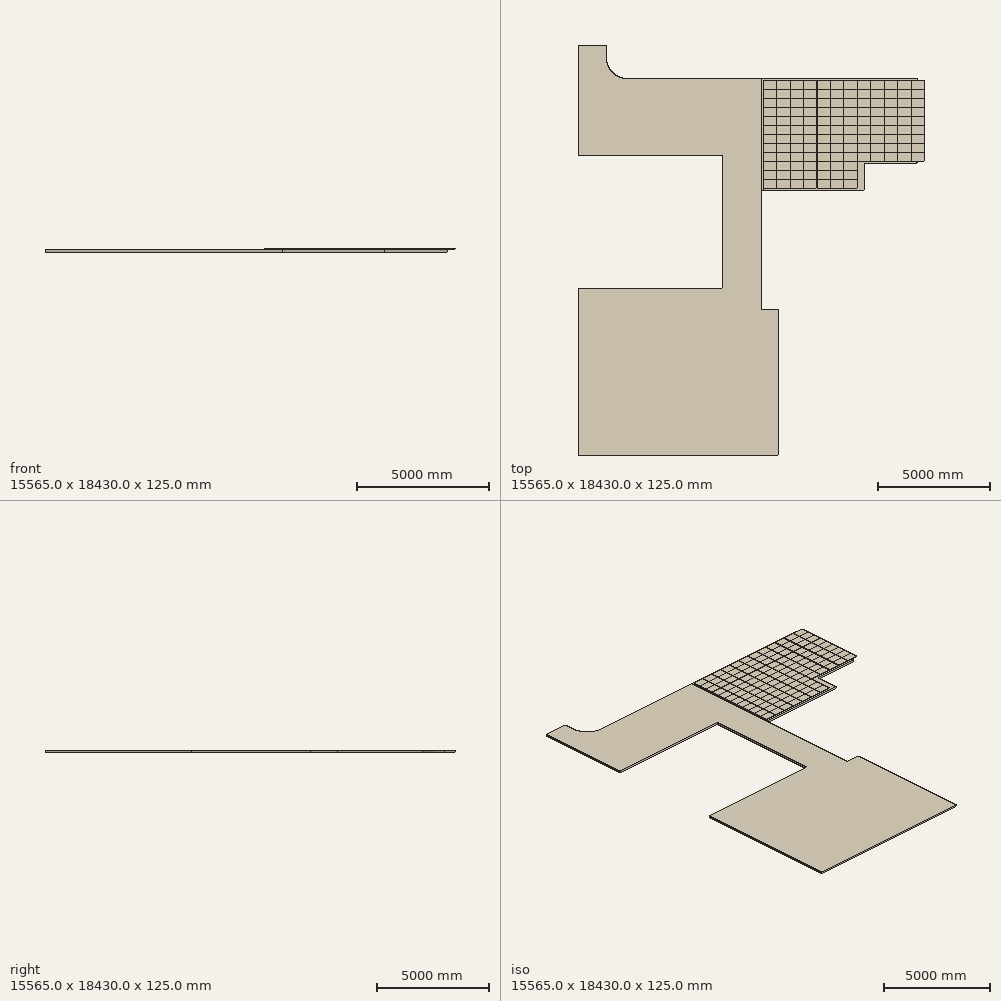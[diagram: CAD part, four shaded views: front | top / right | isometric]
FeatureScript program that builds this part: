
annotation { "Feature Type Name" : "Feature", "Feature Type Description" : "" }
export const myFeature = defineFeature(function(context is Context, id is Id, definition is map)
    precondition{}
    {
        {
            var Q0;
            Q0=qCreatedBy(makeId("Top.planeOp"),FACE);
            var sketch = newSketch(context, id + "F0", { "sketchPlane" : qUnion([Q0])});
            skLineSegment(sketch, "E0.bottom", {"start": v(1925, 8965) * mm, "end": v(-11075, 8965) * mm});
            skLineSegment(sketch, "E0.top", {"start": v(1925, 3965) * mm, "end": v(-5075, 3965) * mm});
            skLineSegment(sketch, "E0.left", {"start": v(1925, 8965) * mm, "end": v(1925, 3965) * mm});
            skLineSegment(sketch, "E0.right", {"start": v(-5075, 3965) * mm, "end": v(-5075, -1415) * mm});
            skLineSegment(sketch, "E1", {"start": v(-6825, 5535) * mm, "end": v(-6825, -465) * mm});
            skLineSegment(sketch, "E2", {"start": v(-4325, -1415) * mm, "end": v(-4325, -7965) * mm});
            skLineSegment(sketch, "E3", {"start": v(-4325, -7965) * mm, "end": v(-13325, -7965) * mm});
            skLineSegment(sketch, "E4", {"start": v(-13325, -7965) * mm, "end": v(-13325, -465) * mm});
            skLineSegment(sketch, "E5", {"start": v(-13325, -465) * mm, "end": v(-6825, -465) * mm});
            skLineSegment(sketch, "E6", {"start": v(-4325, -1415) * mm, "end": v(-5075, -1415) * mm});
            skLineSegment(sketch, "E7.top", {"start": v(-6825, 5535) * mm, "end": v(-13325, 5535) * mm});
            skLineSegment(sketch, "E8", {"start": v(-13325, 5535) * mm, "end": v(-13325, 10465) * mm});
            skLineSegment(sketch, "E9", {"start": v(-12075, 9965) * mm, "end": v(-12075, 10465) * mm});
            skLineSegment(sketch, "E10", {"start": v(-12075, 10465) * mm, "end": v(-13325, 10465) * mm});
            skPoint(sketch, "E11.0.visualSharp", {"position": v(-12075, 8965) * mm});
            skArc(sketch, "E11.0.filletArc", {"start": v(-12075, 9965) * mm, "mid": v(-11782.1, 9257.9) * mm, "end": v(-11075, 8965) * mm});
            skSolve(sketch);
        }
        {
            var Q0;
            Q0=makeQuery(id+"F0.imprint","IMPRINT",FACE,{"disambiguationData":[TD([[makeQuery(id+"F0.imprint","IMPRINT",EDGE,{"derivedFrom":sQuery(id+"F0.wireOp",EDGE,"E0.bottom")}),1.0]])]});
            extrude(context, id + "F1", {"entities" : qUnion([Q0]), "oppositeDirection" : true, "depth" : 100 * mm});
        }
        {
            var Q0;
            Q0=makeQuery(id+"F1.opExtrude","CAP_FACE",FACE,{"disambiguationData":[OSD([sQuery(id+"F0.wireOp",EDGE,"E0.bottom"),sQuery(id+"F0.wireOp",EDGE,"E0.top"),sQuery(id+"F0.wireOp",EDGE,"E0.left"),sQuery(id+"F0.wireOp",EDGE,"E0.right"),sQuery(id+"F0.wireOp",EDGE,"uScAsCd1-O7hj-DaH3-3mnT-VNKRzyi0iVPP"),sQuery(id+"F0.wireOp",EDGE,"ugRH4nXX-NC2v-Y8Qp-Eb5w-qthfwM3VaUrv"),sQuery(id+"F0.wireOp",EDGE,"aPtSS9E7-FlIR-lzfM-v5Z0-DnZjgckhtP2z")])],"isStart":true});
            var sketch = newSketch(context, id + "F2", { "sketchPlane" : qUnion([Q0])});
            skLineSegment(sketch, "E12.bottom", {"start": v(1925, 3965) * mm, "end": v(-450, 3965) * mm});
            skLineSegment(sketch, "E12.top", {"start": v(1925, 5165) * mm, "end": v(-450, 5165) * mm});
            skLineSegment(sketch, "E12.left", {"start": v(1925, 3965) * mm, "end": v(1925, 5165) * mm});
            skLineSegment(sketch, "E12.right", {"start": v(-450, 3965) * mm, "end": v(-450, 5165) * mm});
            skSolve(sketch);
        }
        {
            var Q0;
            Q0=makeQuery(id+"F2.imprint","IMPRINT",FACE,{"disambiguationData":[TD([[makeQuery(id+"F2.imprint","IMPRINT",EDGE,{"derivedFrom":sQuery(id+"F2.wireOp",EDGE,"E12.bottom")}),-1.0]])]});
            extrude(context, id + "F3", {"entities" : qUnion([Q0]), "operationType" : NewBodyOperationType.REMOVE, "endBound" : BoundingType.UP_TO_NEXT, "oppositeDirection" : true, "depth" : 25 * mm});
        }
        {
            var Q0;
            Q0=makeQuery(id+"F1.opExtrude","CAP_FACE",FACE,{"disambiguationData":[OSD([sQuery(id+"F0.wireOp",EDGE,"E0.bottom"),sQuery(id+"F0.wireOp",EDGE,"E0.top"),sQuery(id+"F0.wireOp",EDGE,"E0.left"),sQuery(id+"F0.wireOp",EDGE,"E0.right"),sQuery(id+"F0.wireOp",EDGE,"E1"),sQuery(id+"F0.wireOp",EDGE,"E2"),sQuery(id+"F0.wireOp",EDGE,"E3"),sQuery(id+"F0.wireOp",EDGE,"E4"),sQuery(id+"F0.wireOp",EDGE,"E5"),sQuery(id+"F0.wireOp",EDGE,"E6"),sQuery(id+"F0.wireOp",EDGE,"IaO83Gh2-lnCz-rkBB-go4h-1UUhoPdXk0SL"),sQuery(id+"F0.wireOp",EDGE,"E7.bottom"),sQuery(id+"F0.wireOp",EDGE,"E7.top"),sQuery(id+"F0.wireOp",EDGE,"E7.right")])],"isStart":true});
            var sketch = newSketch(context, id + "F4", { "sketchPlane" : qUnion([Q0])});
            skLineSegment(sketch, "E13.bottom", {"start": v(-5075, 8965) * mm, "end": v(1925, 8965) * mm});
            skLineSegment(sketch, "E14.bottom", {"start": v(1925, 5165) * mm, "end": v(1865, 5165) * mm});
            skLineSegment(sketch, "E14.left", {"start": v(1925, 5165) * mm, "end": v(1925, 8965) * mm});
            skLineSegment(sketch, "E14.right", {"start": v(1865, 5165) * mm, "end": v(1865, 8905) * mm});
            skLineSegment(sketch, "E15.bottom", {"start": v(-5075, 3965) * mm, "end": v(-5015, 3965) * mm});
            skLineSegment(sketch, "E15.left", {"start": v(-5075, 3965) * mm, "end": v(-5075, 8965) * mm});
            skLineSegment(sketch, "E15.right", {"start": v(-5015, 3965) * mm, "end": v(-5015, 8905) * mm});
            skLineSegment(sketch, "E16.trimOffspring", {"start": v(-5015, 8905) * mm, "end": v(1865, 8905) * mm});
            skSolve(sketch);
        }
        {
            var Q0;
            Q0 = qSketchRegion(id + "F4", true);
            extrude(context, id + "F5", {"entities" : qUnion([Q0]), "operationType" : NewBodyOperationType.ADD, "depth" : 5 * mm});
        }
        {
            var Q0;
            {var subQ0=sQuery(id+"F0.wireOp",EDGE,"E0.top");Q0=makeQuery(id+"F5.boolean.opBoolean","SPLIT",FACE,{"disambiguationData":[TD([makeQuery(id+"F3.boolean.opBoolean","COPY",FACE,{"derivedFrom":makeQuery(id+"F3.opExtrude","SWEPT_FACE",FACE,{"disambiguationData":[OSD([sQuery(id+"F2.wireOp",EDGE,"E12.top")])]})})])],"derivedFrom":makeQuery(id+"F1.opExtrude","CAP_FACE",FACE,{"disambiguationData":[OSD([sQuery(id+"F0.wireOp",EDGE,"E0.bottom"),subQ0,sQuery(id+"F0.wireOp",EDGE,"E0.left"),sQuery(id+"F0.wireOp",EDGE,"E0.right"),sQuery(id+"F0.wireOp",EDGE,"E1"),sQuery(id+"F0.wireOp",EDGE,"E2"),sQuery(id+"F0.wireOp",EDGE,"E3"),sQuery(id+"F0.wireOp",EDGE,"E4"),sQuery(id+"F0.wireOp",EDGE,"E5"),sQuery(id+"F0.wireOp",EDGE,"E6"),sQuery(id+"F0.wireOp",EDGE,"E7.top"),sQuery(id+"F0.wireOp",EDGE,"AURVtqG8-NIB2-Ryh4-XiBF-dMKONcv7BB0R"),sQuery(id+"F0.wireOp",EDGE,"Tb1P3ruf-0xxy-VXF0-uDJz-wuIkWxFJXR6I"),sQuery(id+"F0.wireOp",EDGE,"E8")])],"isStart":true})});}
            var sketch = newSketch(context, id + "F6", { "sketchPlane" : qUnion([Q0])});
            skLineSegment(sketch, "E17.bottom", {"start": v(-5015, 8905) * mm, "end": v(-4415, 8905) * mm});
            skLineSegment(sketch, "E17.top", {"start": v(-5015, 8505) * mm, "end": v(-4415, 8505) * mm});
            skLineSegment(sketch, "E17.left", {"start": v(-5015, 8905) * mm, "end": v(-5015, 8505) * mm});
            skLineSegment(sketch, "E17.right", {"start": v(-4415, 8905) * mm, "end": v(-4415, 8505) * mm});
            skLineSegment(sketch, "E18.0.1.0", {"start": v(-5015, 8500) * mm, "end": v(-4415, 8500) * mm});
            skLineSegment(sketch, "E18.0.1.1", {"start": v(-5015, 8100) * mm, "end": v(-4415, 8100) * mm});
            skLineSegment(sketch, "E18.0.1.2", {"start": v(-5015, 8500) * mm, "end": v(-5015, 8100) * mm});
            skLineSegment(sketch, "E18.0.1.3", {"start": v(-4415, 8500) * mm, "end": v(-4415, 8100) * mm});
            skLineSegment(sketch, "E18.0.2.0", {"start": v(-5015, 8095) * mm, "end": v(-4415, 8095) * mm});
            skLineSegment(sketch, "E18.0.2.1", {"start": v(-5015, 7695) * mm, "end": v(-4415, 7695) * mm});
            skLineSegment(sketch, "E18.0.2.2", {"start": v(-5015, 8095) * mm, "end": v(-5015, 7695) * mm});
            skLineSegment(sketch, "E18.0.2.3", {"start": v(-4415, 8095) * mm, "end": v(-4415, 7695) * mm});
            skLineSegment(sketch, "E18.0.3.0", {"start": v(-5015, 7690) * mm, "end": v(-4415, 7690) * mm});
            skLineSegment(sketch, "E18.0.3.1", {"start": v(-5015, 7290) * mm, "end": v(-4415, 7290) * mm});
            skLineSegment(sketch, "E18.0.3.2", {"start": v(-5015, 7690) * mm, "end": v(-5015, 7290) * mm});
            skLineSegment(sketch, "E18.0.3.3", {"start": v(-4415, 7690) * mm, "end": v(-4415, 7290) * mm});
            skLineSegment(sketch, "E18.0.4.0", {"start": v(-5015, 7285) * mm, "end": v(-4415, 7285) * mm});
            skLineSegment(sketch, "E18.0.4.1", {"start": v(-5015, 6885) * mm, "end": v(-4415, 6885) * mm});
            skLineSegment(sketch, "E18.0.4.2", {"start": v(-5015, 7285) * mm, "end": v(-5015, 6885) * mm});
            skLineSegment(sketch, "E18.0.4.3", {"start": v(-4415, 7285) * mm, "end": v(-4415, 6885) * mm});
            skLineSegment(sketch, "E18.0.5.0", {"start": v(-5015, 6880) * mm, "end": v(-4415, 6880) * mm});
            skLineSegment(sketch, "E18.0.5.1", {"start": v(-5015, 6480) * mm, "end": v(-4415, 6480) * mm});
            skLineSegment(sketch, "E18.0.5.2", {"start": v(-5015, 6880) * mm, "end": v(-5015, 6480) * mm});
            skLineSegment(sketch, "E18.0.5.3", {"start": v(-4415, 6880) * mm, "end": v(-4415, 6480) * mm});
            skLineSegment(sketch, "E18.0.6.0", {"start": v(-5015, 6475) * mm, "end": v(-4415, 6475) * mm});
            skLineSegment(sketch, "E18.0.6.1", {"start": v(-5015, 6075) * mm, "end": v(-4415, 6075) * mm});
            skLineSegment(sketch, "E18.0.6.2", {"start": v(-5015, 6475) * mm, "end": v(-5015, 6075) * mm});
            skLineSegment(sketch, "E18.0.6.3", {"start": v(-4415, 6475) * mm, "end": v(-4415, 6075) * mm});
            skLineSegment(sketch, "E18.0.7.0", {"start": v(-5015, 6070) * mm, "end": v(-4415, 6070) * mm});
            skLineSegment(sketch, "E18.0.7.1", {"start": v(-5015, 5670) * mm, "end": v(-4415, 5670) * mm});
            skLineSegment(sketch, "E18.0.7.2", {"start": v(-5015, 6070) * mm, "end": v(-5015, 5670) * mm});
            skLineSegment(sketch, "E18.0.7.3", {"start": v(-4415, 6070) * mm, "end": v(-4415, 5670) * mm});
            skLineSegment(sketch, "E18.0.8.0", {"start": v(-5015, 5665) * mm, "end": v(-4415, 5665) * mm});
            skLineSegment(sketch, "E18.0.8.1", {"start": v(-5015, 5265) * mm, "end": v(-4415, 5265) * mm});
            skLineSegment(sketch, "E18.0.8.2", {"start": v(-5015, 5665) * mm, "end": v(-5015, 5265) * mm});
            skLineSegment(sketch, "E18.0.8.3", {"start": v(-4415, 5665) * mm, "end": v(-4415, 5265) * mm});
            skLineSegment(sketch, "E18.0.9.0", {"start": v(-5015, 5260) * mm, "end": v(-4415, 5260) * mm});
            skLineSegment(sketch, "E18.0.9.1", {"start": v(-5015, 4860) * mm, "end": v(-4415, 4860) * mm});
            skLineSegment(sketch, "E18.0.9.2", {"start": v(-5015, 5260) * mm, "end": v(-5015, 4860) * mm});
            skLineSegment(sketch, "E18.0.9.3", {"start": v(-4415, 5260) * mm, "end": v(-4415, 4860) * mm});
            skLineSegment(sketch, "E18.0.10.0", {"start": v(-5015, 4855) * mm, "end": v(-4415, 4855) * mm});
            skLineSegment(sketch, "E18.0.10.1", {"start": v(-5015, 4455) * mm, "end": v(-4415, 4455) * mm});
            skLineSegment(sketch, "E18.0.10.2", {"start": v(-5015, 4855) * mm, "end": v(-5015, 4455) * mm});
            skLineSegment(sketch, "E18.0.10.3", {"start": v(-4415, 4855) * mm, "end": v(-4415, 4455) * mm});
            skLineSegment(sketch, "E18.0.11.0", {"start": v(-5015, 4450) * mm, "end": v(-4415, 4450) * mm});
            skLineSegment(sketch, "E18.0.11.1", {"start": v(-5015, 4050) * mm, "end": v(-4415, 4050) * mm});
            skLineSegment(sketch, "E18.0.11.2", {"start": v(-5015, 4450) * mm, "end": v(-5015, 4050) * mm});
            skLineSegment(sketch, "E18.0.11.3", {"start": v(-4415, 4450) * mm, "end": v(-4415, 4050) * mm});
            skLineSegment(sketch, "E18.1.0.0", {"start": v(-4410, 8905) * mm, "end": v(-3810, 8905) * mm});
            skLineSegment(sketch, "E18.1.0.1", {"start": v(-4410, 8505) * mm, "end": v(-3810, 8505) * mm});
            skLineSegment(sketch, "E18.1.0.2", {"start": v(-4410, 8905) * mm, "end": v(-4410, 8505) * mm});
            skLineSegment(sketch, "E18.1.0.3", {"start": v(-3810, 8905) * mm, "end": v(-3810, 8505) * mm});
            skLineSegment(sketch, "E18.1.1.0", {"start": v(-4410, 8500) * mm, "end": v(-3810, 8500) * mm});
            skLineSegment(sketch, "E18.1.1.1", {"start": v(-4410, 8100) * mm, "end": v(-3810, 8100) * mm});
            skLineSegment(sketch, "E18.1.1.2", {"start": v(-4410, 8500) * mm, "end": v(-4410, 8100) * mm});
            skLineSegment(sketch, "E18.1.1.3", {"start": v(-3810, 8500) * mm, "end": v(-3810, 8100) * mm});
            skLineSegment(sketch, "E18.1.2.0", {"start": v(-4410, 8095) * mm, "end": v(-3810, 8095) * mm});
            skLineSegment(sketch, "E18.1.2.1", {"start": v(-4410, 7695) * mm, "end": v(-3810, 7695) * mm});
            skLineSegment(sketch, "E18.1.2.2", {"start": v(-4410, 8095) * mm, "end": v(-4410, 7695) * mm});
            skLineSegment(sketch, "E18.1.2.3", {"start": v(-3810, 8095) * mm, "end": v(-3810, 7695) * mm});
            skLineSegment(sketch, "E18.1.3.0", {"start": v(-4410, 7690) * mm, "end": v(-3810, 7690) * mm});
            skLineSegment(sketch, "E18.1.3.1", {"start": v(-4410, 7290) * mm, "end": v(-3810, 7290) * mm});
            skLineSegment(sketch, "E18.1.3.2", {"start": v(-4410, 7690) * mm, "end": v(-4410, 7290) * mm});
            skLineSegment(sketch, "E18.1.3.3", {"start": v(-3810, 7690) * mm, "end": v(-3810, 7290) * mm});
            skLineSegment(sketch, "E18.1.4.0", {"start": v(-4410, 7285) * mm, "end": v(-3810, 7285) * mm});
            skLineSegment(sketch, "E18.1.4.1", {"start": v(-4410, 6885) * mm, "end": v(-3810, 6885) * mm});
            skLineSegment(sketch, "E18.1.4.2", {"start": v(-4410, 7285) * mm, "end": v(-4410, 6885) * mm});
            skLineSegment(sketch, "E18.1.4.3", {"start": v(-3810, 7285) * mm, "end": v(-3810, 6885) * mm});
            skLineSegment(sketch, "E18.1.5.0", {"start": v(-4410, 6880) * mm, "end": v(-3810, 6880) * mm});
            skLineSegment(sketch, "E18.1.5.1", {"start": v(-4410, 6480) * mm, "end": v(-3810, 6480) * mm});
            skLineSegment(sketch, "E18.1.5.2", {"start": v(-4410, 6880) * mm, "end": v(-4410, 6480) * mm});
            skLineSegment(sketch, "E18.1.5.3", {"start": v(-3810, 6880) * mm, "end": v(-3810, 6480) * mm});
            skLineSegment(sketch, "E18.1.6.0", {"start": v(-4410, 6475) * mm, "end": v(-3810, 6475) * mm});
            skLineSegment(sketch, "E18.1.6.1", {"start": v(-4410, 6075) * mm, "end": v(-3810, 6075) * mm});
            skLineSegment(sketch, "E18.1.6.2", {"start": v(-4410, 6475) * mm, "end": v(-4410, 6075) * mm});
            skLineSegment(sketch, "E18.1.6.3", {"start": v(-3810, 6475) * mm, "end": v(-3810, 6075) * mm});
            skLineSegment(sketch, "E18.1.7.0", {"start": v(-4410, 6070) * mm, "end": v(-3810, 6070) * mm});
            skLineSegment(sketch, "E18.1.7.1", {"start": v(-4410, 5670) * mm, "end": v(-3810, 5670) * mm});
            skLineSegment(sketch, "E18.1.7.2", {"start": v(-4410, 6070) * mm, "end": v(-4410, 5670) * mm});
            skLineSegment(sketch, "E18.1.7.3", {"start": v(-3810, 6070) * mm, "end": v(-3810, 5670) * mm});
            skLineSegment(sketch, "E18.1.8.0", {"start": v(-4410, 5665) * mm, "end": v(-3810, 5665) * mm});
            skLineSegment(sketch, "E18.1.8.1", {"start": v(-4410, 5265) * mm, "end": v(-3810, 5265) * mm});
            skLineSegment(sketch, "E18.1.8.2", {"start": v(-4410, 5665) * mm, "end": v(-4410, 5265) * mm});
            skLineSegment(sketch, "E18.1.8.3", {"start": v(-3810, 5665) * mm, "end": v(-3810, 5265) * mm});
            skLineSegment(sketch, "E18.1.9.0", {"start": v(-4410, 5260) * mm, "end": v(-3810, 5260) * mm});
            skLineSegment(sketch, "E18.1.9.1", {"start": v(-4410, 4860) * mm, "end": v(-3810, 4860) * mm});
            skLineSegment(sketch, "E18.1.9.2", {"start": v(-4410, 5260) * mm, "end": v(-4410, 4860) * mm});
            skLineSegment(sketch, "E18.1.9.3", {"start": v(-3810, 5260) * mm, "end": v(-3810, 4860) * mm});
            skLineSegment(sketch, "E18.1.10.0", {"start": v(-4410, 4855) * mm, "end": v(-3810, 4855) * mm});
            skLineSegment(sketch, "E18.1.10.1", {"start": v(-4410, 4455) * mm, "end": v(-3810, 4455) * mm});
            skLineSegment(sketch, "E18.1.10.2", {"start": v(-4410, 4855) * mm, "end": v(-4410, 4455) * mm});
            skLineSegment(sketch, "E18.1.10.3", {"start": v(-3810, 4855) * mm, "end": v(-3810, 4455) * mm});
            skLineSegment(sketch, "E18.1.11.0", {"start": v(-4410, 4450) * mm, "end": v(-3810, 4450) * mm});
            skLineSegment(sketch, "E18.1.11.1", {"start": v(-4410, 4050) * mm, "end": v(-3810, 4050) * mm});
            skLineSegment(sketch, "E18.1.11.2", {"start": v(-4410, 4450) * mm, "end": v(-4410, 4050) * mm});
            skLineSegment(sketch, "E18.1.11.3", {"start": v(-3810, 4450) * mm, "end": v(-3810, 4050) * mm});
            skLineSegment(sketch, "E18.2.0.0", {"start": v(-3805, 8905) * mm, "end": v(-3205, 8905) * mm});
            skLineSegment(sketch, "E18.2.0.1", {"start": v(-3805, 8505) * mm, "end": v(-3205, 8505) * mm});
            skLineSegment(sketch, "E18.2.0.2", {"start": v(-3805, 8905) * mm, "end": v(-3805, 8505) * mm});
            skLineSegment(sketch, "E18.2.0.3", {"start": v(-3205, 8905) * mm, "end": v(-3205, 8505) * mm});
            skLineSegment(sketch, "E18.2.1.0", {"start": v(-3805, 8500) * mm, "end": v(-3205, 8500) * mm});
            skLineSegment(sketch, "E18.2.1.1", {"start": v(-3805, 8100) * mm, "end": v(-3205, 8100) * mm});
            skLineSegment(sketch, "E18.2.1.2", {"start": v(-3805, 8500) * mm, "end": v(-3805, 8100) * mm});
            skLineSegment(sketch, "E18.2.1.3", {"start": v(-3205, 8500) * mm, "end": v(-3205, 8100) * mm});
            skLineSegment(sketch, "E18.2.2.0", {"start": v(-3805, 8095) * mm, "end": v(-3205, 8095) * mm});
            skLineSegment(sketch, "E18.2.2.1", {"start": v(-3805, 7695) * mm, "end": v(-3205, 7695) * mm});
            skLineSegment(sketch, "E18.2.2.2", {"start": v(-3805, 8095) * mm, "end": v(-3805, 7695) * mm});
            skLineSegment(sketch, "E18.2.2.3", {"start": v(-3205, 8095) * mm, "end": v(-3205, 7695) * mm});
            skLineSegment(sketch, "E18.2.3.0", {"start": v(-3805, 7690) * mm, "end": v(-3205, 7690) * mm});
            skLineSegment(sketch, "E18.2.3.1", {"start": v(-3805, 7290) * mm, "end": v(-3205, 7290) * mm});
            skLineSegment(sketch, "E18.2.3.2", {"start": v(-3805, 7690) * mm, "end": v(-3805, 7290) * mm});
            skLineSegment(sketch, "E18.2.3.3", {"start": v(-3205, 7690) * mm, "end": v(-3205, 7290) * mm});
            skLineSegment(sketch, "E18.2.4.0", {"start": v(-3805, 7285) * mm, "end": v(-3205, 7285) * mm});
            skLineSegment(sketch, "E18.2.4.1", {"start": v(-3805, 6885) * mm, "end": v(-3205, 6885) * mm});
            skLineSegment(sketch, "E18.2.4.2", {"start": v(-3805, 7285) * mm, "end": v(-3805, 6885) * mm});
            skLineSegment(sketch, "E18.2.4.3", {"start": v(-3205, 7285) * mm, "end": v(-3205, 6885) * mm});
            skLineSegment(sketch, "E18.2.5.0", {"start": v(-3805, 6880) * mm, "end": v(-3205, 6880) * mm});
            skLineSegment(sketch, "E18.2.5.1", {"start": v(-3805, 6480) * mm, "end": v(-3205, 6480) * mm});
            skLineSegment(sketch, "E18.2.5.2", {"start": v(-3805, 6880) * mm, "end": v(-3805, 6480) * mm});
            skLineSegment(sketch, "E18.2.5.3", {"start": v(-3205, 6880) * mm, "end": v(-3205, 6480) * mm});
            skLineSegment(sketch, "E18.2.6.0", {"start": v(-3805, 6475) * mm, "end": v(-3205, 6475) * mm});
            skLineSegment(sketch, "E18.2.6.1", {"start": v(-3805, 6075) * mm, "end": v(-3205, 6075) * mm});
            skLineSegment(sketch, "E18.2.6.2", {"start": v(-3805, 6475) * mm, "end": v(-3805, 6075) * mm});
            skLineSegment(sketch, "E18.2.6.3", {"start": v(-3205, 6475) * mm, "end": v(-3205, 6075) * mm});
            skLineSegment(sketch, "E18.2.7.0", {"start": v(-3805, 6070) * mm, "end": v(-3205, 6070) * mm});
            skLineSegment(sketch, "E18.2.7.1", {"start": v(-3805, 5670) * mm, "end": v(-3205, 5670) * mm});
            skLineSegment(sketch, "E18.2.7.2", {"start": v(-3805, 6070) * mm, "end": v(-3805, 5670) * mm});
            skLineSegment(sketch, "E18.2.7.3", {"start": v(-3205, 6070) * mm, "end": v(-3205, 5670) * mm});
            skLineSegment(sketch, "E18.2.8.0", {"start": v(-3805, 5665) * mm, "end": v(-3205, 5665) * mm});
            skLineSegment(sketch, "E18.2.8.1", {"start": v(-3805, 5265) * mm, "end": v(-3205, 5265) * mm});
            skLineSegment(sketch, "E18.2.8.2", {"start": v(-3805, 5665) * mm, "end": v(-3805, 5265) * mm});
            skLineSegment(sketch, "E18.2.8.3", {"start": v(-3205, 5665) * mm, "end": v(-3205, 5265) * mm});
            skLineSegment(sketch, "E18.2.9.0", {"start": v(-3805, 5260) * mm, "end": v(-3205, 5260) * mm});
            skLineSegment(sketch, "E18.2.9.1", {"start": v(-3805, 4860) * mm, "end": v(-3205, 4860) * mm});
            skLineSegment(sketch, "E18.2.9.2", {"start": v(-3805, 5260) * mm, "end": v(-3805, 4860) * mm});
            skLineSegment(sketch, "E18.2.9.3", {"start": v(-3205, 5260) * mm, "end": v(-3205, 4860) * mm});
            skLineSegment(sketch, "E18.2.10.0", {"start": v(-3805, 4855) * mm, "end": v(-3205, 4855) * mm});
            skLineSegment(sketch, "E18.2.10.1", {"start": v(-3805, 4455) * mm, "end": v(-3205, 4455) * mm});
            skLineSegment(sketch, "E18.2.10.2", {"start": v(-3805, 4855) * mm, "end": v(-3805, 4455) * mm});
            skLineSegment(sketch, "E18.2.10.3", {"start": v(-3205, 4855) * mm, "end": v(-3205, 4455) * mm});
            skLineSegment(sketch, "E18.2.11.0", {"start": v(-3805, 4450) * mm, "end": v(-3205, 4450) * mm});
            skLineSegment(sketch, "E18.2.11.1", {"start": v(-3805, 4050) * mm, "end": v(-3205, 4050) * mm});
            skLineSegment(sketch, "E18.2.11.2", {"start": v(-3805, 4450) * mm, "end": v(-3805, 4050) * mm});
            skLineSegment(sketch, "E18.2.11.3", {"start": v(-3205, 4450) * mm, "end": v(-3205, 4050) * mm});
            skLineSegment(sketch, "E18.3.0.0", {"start": v(-3200, 8905) * mm, "end": v(-2600, 8905) * mm});
            skLineSegment(sketch, "E18.3.0.1", {"start": v(-3200, 8505) * mm, "end": v(-2600, 8505) * mm});
            skLineSegment(sketch, "E18.3.0.2", {"start": v(-3200, 8905) * mm, "end": v(-3200, 8505) * mm});
            skLineSegment(sketch, "E18.3.0.3", {"start": v(-2600, 8905) * mm, "end": v(-2600, 8505) * mm});
            skLineSegment(sketch, "E18.3.1.0", {"start": v(-3200, 8500) * mm, "end": v(-2600, 8500) * mm});
            skLineSegment(sketch, "E18.3.1.1", {"start": v(-3200, 8100) * mm, "end": v(-2600, 8100) * mm});
            skLineSegment(sketch, "E18.3.1.2", {"start": v(-3200, 8500) * mm, "end": v(-3200, 8100) * mm});
            skLineSegment(sketch, "E18.3.1.3", {"start": v(-2600, 8500) * mm, "end": v(-2600, 8100) * mm});
            skLineSegment(sketch, "E18.3.2.0", {"start": v(-3200, 8095) * mm, "end": v(-2600, 8095) * mm});
            skLineSegment(sketch, "E18.3.2.1", {"start": v(-3200, 7695) * mm, "end": v(-2600, 7695) * mm});
            skLineSegment(sketch, "E18.3.2.2", {"start": v(-3200, 8095) * mm, "end": v(-3200, 7695) * mm});
            skLineSegment(sketch, "E18.3.2.3", {"start": v(-2600, 8095) * mm, "end": v(-2600, 7695) * mm});
            skLineSegment(sketch, "E18.3.3.0", {"start": v(-3200, 7690) * mm, "end": v(-2600, 7690) * mm});
            skLineSegment(sketch, "E18.3.3.1", {"start": v(-3200, 7290) * mm, "end": v(-2600, 7290) * mm});
            skLineSegment(sketch, "E18.3.3.2", {"start": v(-3200, 7690) * mm, "end": v(-3200, 7290) * mm});
            skLineSegment(sketch, "E18.3.3.3", {"start": v(-2600, 7690) * mm, "end": v(-2600, 7290) * mm});
            skLineSegment(sketch, "E18.3.4.0", {"start": v(-3200, 7285) * mm, "end": v(-2600, 7285) * mm});
            skLineSegment(sketch, "E18.3.4.1", {"start": v(-3200, 6885) * mm, "end": v(-2600, 6885) * mm});
            skLineSegment(sketch, "E18.3.4.2", {"start": v(-3200, 7285) * mm, "end": v(-3200, 6885) * mm});
            skLineSegment(sketch, "E18.3.4.3", {"start": v(-2600, 7285) * mm, "end": v(-2600, 6885) * mm});
            skLineSegment(sketch, "E18.3.5.0", {"start": v(-3200, 6880) * mm, "end": v(-2600, 6880) * mm});
            skLineSegment(sketch, "E18.3.5.1", {"start": v(-3200, 6480) * mm, "end": v(-2600, 6480) * mm});
            skLineSegment(sketch, "E18.3.5.2", {"start": v(-3200, 6880) * mm, "end": v(-3200, 6480) * mm});
            skLineSegment(sketch, "E18.3.5.3", {"start": v(-2600, 6880) * mm, "end": v(-2600, 6480) * mm});
            skLineSegment(sketch, "E18.3.6.0", {"start": v(-3200, 6475) * mm, "end": v(-2600, 6475) * mm});
            skLineSegment(sketch, "E18.3.6.1", {"start": v(-3200, 6075) * mm, "end": v(-2600, 6075) * mm});
            skLineSegment(sketch, "E18.3.6.2", {"start": v(-3200, 6475) * mm, "end": v(-3200, 6075) * mm});
            skLineSegment(sketch, "E18.3.6.3", {"start": v(-2600, 6475) * mm, "end": v(-2600, 6075) * mm});
            skLineSegment(sketch, "E18.3.7.0", {"start": v(-3200, 6070) * mm, "end": v(-2600, 6070) * mm});
            skLineSegment(sketch, "E18.3.7.1", {"start": v(-3200, 5670) * mm, "end": v(-2600, 5670) * mm});
            skLineSegment(sketch, "E18.3.7.2", {"start": v(-3200, 6070) * mm, "end": v(-3200, 5670) * mm});
            skLineSegment(sketch, "E18.3.7.3", {"start": v(-2600, 6070) * mm, "end": v(-2600, 5670) * mm});
            skLineSegment(sketch, "E18.3.8.0", {"start": v(-3200, 5665) * mm, "end": v(-2600, 5665) * mm});
            skLineSegment(sketch, "E18.3.8.1", {"start": v(-3200, 5265) * mm, "end": v(-2600, 5265) * mm});
            skLineSegment(sketch, "E18.3.8.2", {"start": v(-3200, 5665) * mm, "end": v(-3200, 5265) * mm});
            skLineSegment(sketch, "E18.3.8.3", {"start": v(-2600, 5665) * mm, "end": v(-2600, 5265) * mm});
            skLineSegment(sketch, "E18.3.9.0", {"start": v(-3200, 5260) * mm, "end": v(-2600, 5260) * mm});
            skLineSegment(sketch, "E18.3.9.1", {"start": v(-3200, 4860) * mm, "end": v(-2600, 4860) * mm});
            skLineSegment(sketch, "E18.3.9.2", {"start": v(-3200, 5260) * mm, "end": v(-3200, 4860) * mm});
            skLineSegment(sketch, "E18.3.9.3", {"start": v(-2600, 5260) * mm, "end": v(-2600, 4860) * mm});
            skLineSegment(sketch, "E18.3.10.0", {"start": v(-3200, 4855) * mm, "end": v(-2600, 4855) * mm});
            skLineSegment(sketch, "E18.3.10.1", {"start": v(-3200, 4455) * mm, "end": v(-2600, 4455) * mm});
            skLineSegment(sketch, "E18.3.10.2", {"start": v(-3200, 4855) * mm, "end": v(-3200, 4455) * mm});
            skLineSegment(sketch, "E18.3.10.3", {"start": v(-2600, 4855) * mm, "end": v(-2600, 4455) * mm});
            skLineSegment(sketch, "E18.3.11.0", {"start": v(-3200, 4450) * mm, "end": v(-2600, 4450) * mm});
            skLineSegment(sketch, "E18.3.11.1", {"start": v(-3200, 4050) * mm, "end": v(-2600, 4050) * mm});
            skLineSegment(sketch, "E18.3.11.2", {"start": v(-3200, 4450) * mm, "end": v(-3200, 4050) * mm});
            skLineSegment(sketch, "E18.3.11.3", {"start": v(-2600, 4450) * mm, "end": v(-2600, 4050) * mm});
            skLineSegment(sketch, "E18.4.0.0", {"start": v(-2595, 8905) * mm, "end": v(-1995, 8905) * mm});
            skLineSegment(sketch, "E18.4.0.1", {"start": v(-2595, 8505) * mm, "end": v(-1995, 8505) * mm});
            skLineSegment(sketch, "E18.4.0.2", {"start": v(-2595, 8905) * mm, "end": v(-2595, 8505) * mm});
            skLineSegment(sketch, "E18.4.0.3", {"start": v(-1995, 8905) * mm, "end": v(-1995, 8505) * mm});
            skLineSegment(sketch, "E18.4.1.0", {"start": v(-2595, 8500) * mm, "end": v(-1995, 8500) * mm});
            skLineSegment(sketch, "E18.4.1.1", {"start": v(-2595, 8100) * mm, "end": v(-1995, 8100) * mm});
            skLineSegment(sketch, "E18.4.1.2", {"start": v(-2595, 8500) * mm, "end": v(-2595, 8100) * mm});
            skLineSegment(sketch, "E18.4.1.3", {"start": v(-1995, 8500) * mm, "end": v(-1995, 8100) * mm});
            skLineSegment(sketch, "E18.4.2.0", {"start": v(-2595, 8095) * mm, "end": v(-1995, 8095) * mm});
            skLineSegment(sketch, "E18.4.2.1", {"start": v(-2595, 7695) * mm, "end": v(-1995, 7695) * mm});
            skLineSegment(sketch, "E18.4.2.2", {"start": v(-2595, 8095) * mm, "end": v(-2595, 7695) * mm});
            skLineSegment(sketch, "E18.4.2.3", {"start": v(-1995, 8095) * mm, "end": v(-1995, 7695) * mm});
            skLineSegment(sketch, "E18.4.3.0", {"start": v(-2595, 7690) * mm, "end": v(-1995, 7690) * mm});
            skLineSegment(sketch, "E18.4.3.1", {"start": v(-2595, 7290) * mm, "end": v(-1995, 7290) * mm});
            skLineSegment(sketch, "E18.4.3.2", {"start": v(-2595, 7690) * mm, "end": v(-2595, 7290) * mm});
            skLineSegment(sketch, "E18.4.3.3", {"start": v(-1995, 7690) * mm, "end": v(-1995, 7290) * mm});
            skLineSegment(sketch, "E18.4.4.0", {"start": v(-2595, 7285) * mm, "end": v(-1995, 7285) * mm});
            skLineSegment(sketch, "E18.4.4.1", {"start": v(-2595, 6885) * mm, "end": v(-1995, 6885) * mm});
            skLineSegment(sketch, "E18.4.4.2", {"start": v(-2595, 7285) * mm, "end": v(-2595, 6885) * mm});
            skLineSegment(sketch, "E18.4.4.3", {"start": v(-1995, 7285) * mm, "end": v(-1995, 6885) * mm});
            skLineSegment(sketch, "E18.4.5.0", {"start": v(-2595, 6880) * mm, "end": v(-1995, 6880) * mm});
            skLineSegment(sketch, "E18.4.5.1", {"start": v(-2595, 6480) * mm, "end": v(-1995, 6480) * mm});
            skLineSegment(sketch, "E18.4.5.2", {"start": v(-2595, 6880) * mm, "end": v(-2595, 6480) * mm});
            skLineSegment(sketch, "E18.4.5.3", {"start": v(-1995, 6880) * mm, "end": v(-1995, 6480) * mm});
            skLineSegment(sketch, "E18.4.6.0", {"start": v(-2595, 6475) * mm, "end": v(-1995, 6475) * mm});
            skLineSegment(sketch, "E18.4.6.1", {"start": v(-2595, 6075) * mm, "end": v(-1995, 6075) * mm});
            skLineSegment(sketch, "E18.4.6.2", {"start": v(-2595, 6475) * mm, "end": v(-2595, 6075) * mm});
            skLineSegment(sketch, "E18.4.6.3", {"start": v(-1995, 6475) * mm, "end": v(-1995, 6075) * mm});
            skLineSegment(sketch, "E18.4.7.0", {"start": v(-2595, 6070) * mm, "end": v(-1995, 6070) * mm});
            skLineSegment(sketch, "E18.4.7.1", {"start": v(-2595, 5670) * mm, "end": v(-1995, 5670) * mm});
            skLineSegment(sketch, "E18.4.7.2", {"start": v(-2595, 6070) * mm, "end": v(-2595, 5670) * mm});
            skLineSegment(sketch, "E18.4.7.3", {"start": v(-1995, 6070) * mm, "end": v(-1995, 5670) * mm});
            skLineSegment(sketch, "E18.4.8.0", {"start": v(-2595, 5665) * mm, "end": v(-1995, 5665) * mm});
            skLineSegment(sketch, "E18.4.8.1", {"start": v(-2595, 5265) * mm, "end": v(-1995, 5265) * mm});
            skLineSegment(sketch, "E18.4.8.2", {"start": v(-2595, 5665) * mm, "end": v(-2595, 5265) * mm});
            skLineSegment(sketch, "E18.4.8.3", {"start": v(-1995, 5665) * mm, "end": v(-1995, 5265) * mm});
            skLineSegment(sketch, "E18.4.9.0", {"start": v(-2595, 5260) * mm, "end": v(-1995, 5260) * mm});
            skLineSegment(sketch, "E18.4.9.1", {"start": v(-2595, 4860) * mm, "end": v(-1995, 4860) * mm});
            skLineSegment(sketch, "E18.4.9.2", {"start": v(-2595, 5260) * mm, "end": v(-2595, 4860) * mm});
            skLineSegment(sketch, "E18.4.9.3", {"start": v(-1995, 5260) * mm, "end": v(-1995, 4860) * mm});
            skLineSegment(sketch, "E18.4.10.0", {"start": v(-2595, 4855) * mm, "end": v(-1995, 4855) * mm});
            skLineSegment(sketch, "E18.4.10.1", {"start": v(-2595, 4455) * mm, "end": v(-1995, 4455) * mm});
            skLineSegment(sketch, "E18.4.10.2", {"start": v(-2595, 4855) * mm, "end": v(-2595, 4455) * mm});
            skLineSegment(sketch, "E18.4.10.3", {"start": v(-1995, 4855) * mm, "end": v(-1995, 4455) * mm});
            skLineSegment(sketch, "E18.4.11.0", {"start": v(-2595, 4450) * mm, "end": v(-1995, 4450) * mm});
            skLineSegment(sketch, "E18.4.11.1", {"start": v(-2595, 4050) * mm, "end": v(-1995, 4050) * mm});
            skLineSegment(sketch, "E18.4.11.2", {"start": v(-2595, 4450) * mm, "end": v(-2595, 4050) * mm});
            skLineSegment(sketch, "E18.4.11.3", {"start": v(-1995, 4450) * mm, "end": v(-1995, 4050) * mm});
            skLineSegment(sketch, "E18.5.0.0", {"start": v(-1990, 8905) * mm, "end": v(-1390, 8905) * mm});
            skLineSegment(sketch, "E18.5.0.1", {"start": v(-1990, 8505) * mm, "end": v(-1390, 8505) * mm});
            skLineSegment(sketch, "E18.5.0.2", {"start": v(-1990, 8905) * mm, "end": v(-1990, 8505) * mm});
            skLineSegment(sketch, "E18.5.0.3", {"start": v(-1390, 8905) * mm, "end": v(-1390, 8505) * mm});
            skLineSegment(sketch, "E18.5.1.0", {"start": v(-1990, 8500) * mm, "end": v(-1390, 8500) * mm});
            skLineSegment(sketch, "E18.5.1.1", {"start": v(-1990, 8100) * mm, "end": v(-1390, 8100) * mm});
            skLineSegment(sketch, "E18.5.1.2", {"start": v(-1990, 8500) * mm, "end": v(-1990, 8100) * mm});
            skLineSegment(sketch, "E18.5.1.3", {"start": v(-1390, 8500) * mm, "end": v(-1390, 8100) * mm});
            skLineSegment(sketch, "E18.5.2.0", {"start": v(-1990, 8095) * mm, "end": v(-1390, 8095) * mm});
            skLineSegment(sketch, "E18.5.2.1", {"start": v(-1990, 7695) * mm, "end": v(-1390, 7695) * mm});
            skLineSegment(sketch, "E18.5.2.2", {"start": v(-1990, 8095) * mm, "end": v(-1990, 7695) * mm});
            skLineSegment(sketch, "E18.5.2.3", {"start": v(-1390, 8095) * mm, "end": v(-1390, 7695) * mm});
            skLineSegment(sketch, "E18.5.3.0", {"start": v(-1990, 7690) * mm, "end": v(-1390, 7690) * mm});
            skLineSegment(sketch, "E18.5.3.1", {"start": v(-1990, 7290) * mm, "end": v(-1390, 7290) * mm});
            skLineSegment(sketch, "E18.5.3.2", {"start": v(-1990, 7690) * mm, "end": v(-1990, 7290) * mm});
            skLineSegment(sketch, "E18.5.3.3", {"start": v(-1390, 7690) * mm, "end": v(-1390, 7290) * mm});
            skLineSegment(sketch, "E18.5.4.0", {"start": v(-1990, 7285) * mm, "end": v(-1390, 7285) * mm});
            skLineSegment(sketch, "E18.5.4.1", {"start": v(-1990, 6885) * mm, "end": v(-1390, 6885) * mm});
            skLineSegment(sketch, "E18.5.4.2", {"start": v(-1990, 7285) * mm, "end": v(-1990, 6885) * mm});
            skLineSegment(sketch, "E18.5.4.3", {"start": v(-1390, 7285) * mm, "end": v(-1390, 6885) * mm});
            skLineSegment(sketch, "E18.5.5.0", {"start": v(-1990, 6880) * mm, "end": v(-1390, 6880) * mm});
            skLineSegment(sketch, "E18.5.5.1", {"start": v(-1990, 6480) * mm, "end": v(-1390, 6480) * mm});
            skLineSegment(sketch, "E18.5.5.2", {"start": v(-1990, 6880) * mm, "end": v(-1990, 6480) * mm});
            skLineSegment(sketch, "E18.5.5.3", {"start": v(-1390, 6880) * mm, "end": v(-1390, 6480) * mm});
            skLineSegment(sketch, "E18.5.6.0", {"start": v(-1990, 6475) * mm, "end": v(-1390, 6475) * mm});
            skLineSegment(sketch, "E18.5.6.1", {"start": v(-1990, 6075) * mm, "end": v(-1390, 6075) * mm});
            skLineSegment(sketch, "E18.5.6.2", {"start": v(-1990, 6475) * mm, "end": v(-1990, 6075) * mm});
            skLineSegment(sketch, "E18.5.6.3", {"start": v(-1390, 6475) * mm, "end": v(-1390, 6075) * mm});
            skLineSegment(sketch, "E18.5.7.0", {"start": v(-1990, 6070) * mm, "end": v(-1390, 6070) * mm});
            skLineSegment(sketch, "E18.5.7.1", {"start": v(-1990, 5670) * mm, "end": v(-1390, 5670) * mm});
            skLineSegment(sketch, "E18.5.7.2", {"start": v(-1990, 6070) * mm, "end": v(-1990, 5670) * mm});
            skLineSegment(sketch, "E18.5.7.3", {"start": v(-1390, 6070) * mm, "end": v(-1390, 5670) * mm});
            skLineSegment(sketch, "E18.5.8.0", {"start": v(-1990, 5665) * mm, "end": v(-1390, 5665) * mm});
            skLineSegment(sketch, "E18.5.8.1", {"start": v(-1990, 5265) * mm, "end": v(-1390, 5265) * mm});
            skLineSegment(sketch, "E18.5.8.2", {"start": v(-1990, 5665) * mm, "end": v(-1990, 5265) * mm});
            skLineSegment(sketch, "E18.5.8.3", {"start": v(-1390, 5665) * mm, "end": v(-1390, 5265) * mm});
            skLineSegment(sketch, "E18.5.9.0", {"start": v(-1990, 5260) * mm, "end": v(-1390, 5260) * mm});
            skLineSegment(sketch, "E18.5.9.1", {"start": v(-1990, 4860) * mm, "end": v(-1390, 4860) * mm});
            skLineSegment(sketch, "E18.5.9.2", {"start": v(-1990, 5260) * mm, "end": v(-1990, 4860) * mm});
            skLineSegment(sketch, "E18.5.9.3", {"start": v(-1390, 5260) * mm, "end": v(-1390, 4860) * mm});
            skLineSegment(sketch, "E18.5.10.0", {"start": v(-1990, 4855) * mm, "end": v(-1390, 4855) * mm});
            skLineSegment(sketch, "E18.5.10.1", {"start": v(-1990, 4455) * mm, "end": v(-1390, 4455) * mm});
            skLineSegment(sketch, "E18.5.10.2", {"start": v(-1990, 4855) * mm, "end": v(-1990, 4455) * mm});
            skLineSegment(sketch, "E18.5.10.3", {"start": v(-1390, 4855) * mm, "end": v(-1390, 4455) * mm});
            skLineSegment(sketch, "E18.5.11.0", {"start": v(-1990, 4450) * mm, "end": v(-1390, 4450) * mm});
            skLineSegment(sketch, "E18.5.11.1", {"start": v(-1990, 4050) * mm, "end": v(-1390, 4050) * mm});
            skLineSegment(sketch, "E18.5.11.2", {"start": v(-1990, 4450) * mm, "end": v(-1990, 4050) * mm});
            skLineSegment(sketch, "E18.5.11.3", {"start": v(-1390, 4450) * mm, "end": v(-1390, 4050) * mm});
            skLineSegment(sketch, "E18.6.0.0", {"start": v(-1385, 8905) * mm, "end": v(-785, 8905) * mm});
            skLineSegment(sketch, "E18.6.0.1", {"start": v(-1385, 8505) * mm, "end": v(-785, 8505) * mm});
            skLineSegment(sketch, "E18.6.0.2", {"start": v(-1385, 8905) * mm, "end": v(-1385, 8505) * mm});
            skLineSegment(sketch, "E18.6.0.3", {"start": v(-785, 8905) * mm, "end": v(-785, 8505) * mm});
            skLineSegment(sketch, "E18.6.1.0", {"start": v(-1385, 8500) * mm, "end": v(-785, 8500) * mm});
            skLineSegment(sketch, "E18.6.1.1", {"start": v(-1385, 8100) * mm, "end": v(-785, 8100) * mm});
            skLineSegment(sketch, "E18.6.1.2", {"start": v(-1385, 8500) * mm, "end": v(-1385, 8100) * mm});
            skLineSegment(sketch, "E18.6.1.3", {"start": v(-785, 8500) * mm, "end": v(-785, 8100) * mm});
            skLineSegment(sketch, "E18.6.2.0", {"start": v(-1385, 8095) * mm, "end": v(-785, 8095) * mm});
            skLineSegment(sketch, "E18.6.2.1", {"start": v(-1385, 7695) * mm, "end": v(-785, 7695) * mm});
            skLineSegment(sketch, "E18.6.2.2", {"start": v(-1385, 8095) * mm, "end": v(-1385, 7695) * mm});
            skLineSegment(sketch, "E18.6.2.3", {"start": v(-785, 8095) * mm, "end": v(-785, 7695) * mm});
            skLineSegment(sketch, "E18.6.3.0", {"start": v(-1385, 7690) * mm, "end": v(-785, 7690) * mm});
            skLineSegment(sketch, "E18.6.3.1", {"start": v(-1385, 7290) * mm, "end": v(-785, 7290) * mm});
            skLineSegment(sketch, "E18.6.3.2", {"start": v(-1385, 7690) * mm, "end": v(-1385, 7290) * mm});
            skLineSegment(sketch, "E18.6.3.3", {"start": v(-785, 7690) * mm, "end": v(-785, 7290) * mm});
            skLineSegment(sketch, "E18.6.4.0", {"start": v(-1385, 7285) * mm, "end": v(-785, 7285) * mm});
            skLineSegment(sketch, "E18.6.4.1", {"start": v(-1385, 6885) * mm, "end": v(-785, 6885) * mm});
            skLineSegment(sketch, "E18.6.4.2", {"start": v(-1385, 7285) * mm, "end": v(-1385, 6885) * mm});
            skLineSegment(sketch, "E18.6.4.3", {"start": v(-785, 7285) * mm, "end": v(-785, 6885) * mm});
            skLineSegment(sketch, "E18.6.5.0", {"start": v(-1385, 6880) * mm, "end": v(-785, 6880) * mm});
            skLineSegment(sketch, "E18.6.5.1", {"start": v(-1385, 6480) * mm, "end": v(-785, 6480) * mm});
            skLineSegment(sketch, "E18.6.5.2", {"start": v(-1385, 6880) * mm, "end": v(-1385, 6480) * mm});
            skLineSegment(sketch, "E18.6.5.3", {"start": v(-785, 6880) * mm, "end": v(-785, 6480) * mm});
            skLineSegment(sketch, "E18.6.6.0", {"start": v(-1385, 6475) * mm, "end": v(-785, 6475) * mm});
            skLineSegment(sketch, "E18.6.6.1", {"start": v(-1385, 6075) * mm, "end": v(-785, 6075) * mm});
            skLineSegment(sketch, "E18.6.6.2", {"start": v(-1385, 6475) * mm, "end": v(-1385, 6075) * mm});
            skLineSegment(sketch, "E18.6.6.3", {"start": v(-785, 6475) * mm, "end": v(-785, 6075) * mm});
            skLineSegment(sketch, "E18.6.7.0", {"start": v(-1385, 6070) * mm, "end": v(-785, 6070) * mm});
            skLineSegment(sketch, "E18.6.7.1", {"start": v(-1385, 5670) * mm, "end": v(-785, 5670) * mm});
            skLineSegment(sketch, "E18.6.7.2", {"start": v(-1385, 6070) * mm, "end": v(-1385, 5670) * mm});
            skLineSegment(sketch, "E18.6.7.3", {"start": v(-785, 6070) * mm, "end": v(-785, 5670) * mm});
            skLineSegment(sketch, "E18.6.8.0", {"start": v(-1385, 5665) * mm, "end": v(-785, 5665) * mm});
            skLineSegment(sketch, "E18.6.8.1", {"start": v(-1385, 5265) * mm, "end": v(-785, 5265) * mm});
            skLineSegment(sketch, "E18.6.8.2", {"start": v(-1385, 5665) * mm, "end": v(-1385, 5265) * mm});
            skLineSegment(sketch, "E18.6.8.3", {"start": v(-785, 5665) * mm, "end": v(-785, 5265) * mm});
            skLineSegment(sketch, "E18.6.9.0", {"start": v(-1385, 5260) * mm, "end": v(-785, 5260) * mm});
            skLineSegment(sketch, "E18.6.9.1", {"start": v(-1385, 4860) * mm, "end": v(-785, 4860) * mm});
            skLineSegment(sketch, "E18.6.9.2", {"start": v(-1385, 5260) * mm, "end": v(-1385, 4860) * mm});
            skLineSegment(sketch, "E18.6.9.3", {"start": v(-785, 5260) * mm, "end": v(-785, 4860) * mm});
            skLineSegment(sketch, "E18.6.10.0", {"start": v(-1385, 4855) * mm, "end": v(-785, 4855) * mm});
            skLineSegment(sketch, "E18.6.10.1", {"start": v(-1385, 4455) * mm, "end": v(-785, 4455) * mm});
            skLineSegment(sketch, "E18.6.10.2", {"start": v(-1385, 4855) * mm, "end": v(-1385, 4455) * mm});
            skLineSegment(sketch, "E18.6.10.3", {"start": v(-785, 4855) * mm, "end": v(-785, 4455) * mm});
            skLineSegment(sketch, "E18.6.11.0", {"start": v(-1385, 4450) * mm, "end": v(-785, 4450) * mm});
            skLineSegment(sketch, "E18.6.11.1", {"start": v(-1385, 4050) * mm, "end": v(-785, 4050) * mm});
            skLineSegment(sketch, "E18.6.11.2", {"start": v(-1385, 4450) * mm, "end": v(-1385, 4050) * mm});
            skLineSegment(sketch, "E18.6.11.3", {"start": v(-785, 4450) * mm, "end": v(-785, 4050) * mm});
            skLineSegment(sketch, "E18.7.0.0", {"start": v(-780, 8905) * mm, "end": v(-180, 8905) * mm});
            skLineSegment(sketch, "E18.7.0.1", {"start": v(-780, 8505) * mm, "end": v(-180, 8505) * mm});
            skLineSegment(sketch, "E18.7.0.2", {"start": v(-780, 8905) * mm, "end": v(-780, 8505) * mm});
            skLineSegment(sketch, "E18.7.0.3", {"start": v(-180, 8905) * mm, "end": v(-180, 8505) * mm});
            skLineSegment(sketch, "E18.7.1.0", {"start": v(-780, 8500) * mm, "end": v(-180, 8500) * mm});
            skLineSegment(sketch, "E18.7.1.1", {"start": v(-780, 8100) * mm, "end": v(-180, 8100) * mm});
            skLineSegment(sketch, "E18.7.1.2", {"start": v(-780, 8500) * mm, "end": v(-780, 8100) * mm});
            skLineSegment(sketch, "E18.7.1.3", {"start": v(-180, 8500) * mm, "end": v(-180, 8100) * mm});
            skLineSegment(sketch, "E18.7.2.0", {"start": v(-780, 8095) * mm, "end": v(-180, 8095) * mm});
            skLineSegment(sketch, "E18.7.2.1", {"start": v(-780, 7695) * mm, "end": v(-180, 7695) * mm});
            skLineSegment(sketch, "E18.7.2.2", {"start": v(-780, 8095) * mm, "end": v(-780, 7695) * mm});
            skLineSegment(sketch, "E18.7.2.3", {"start": v(-180, 8095) * mm, "end": v(-180, 7695) * mm});
            skLineSegment(sketch, "E18.7.3.0", {"start": v(-780, 7690) * mm, "end": v(-180, 7690) * mm});
            skLineSegment(sketch, "E18.7.3.1", {"start": v(-780, 7290) * mm, "end": v(-180, 7290) * mm});
            skLineSegment(sketch, "E18.7.3.2", {"start": v(-780, 7690) * mm, "end": v(-780, 7290) * mm});
            skLineSegment(sketch, "E18.7.3.3", {"start": v(-180, 7690) * mm, "end": v(-180, 7290) * mm});
            skLineSegment(sketch, "E18.7.4.0", {"start": v(-780, 7285) * mm, "end": v(-180, 7285) * mm});
            skLineSegment(sketch, "E18.7.4.1", {"start": v(-780, 6885) * mm, "end": v(-180, 6885) * mm});
            skLineSegment(sketch, "E18.7.4.2", {"start": v(-780, 7285) * mm, "end": v(-780, 6885) * mm});
            skLineSegment(sketch, "E18.7.4.3", {"start": v(-180, 7285) * mm, "end": v(-180, 6885) * mm});
            skLineSegment(sketch, "E18.7.5.0", {"start": v(-780, 6880) * mm, "end": v(-180, 6880) * mm});
            skLineSegment(sketch, "E18.7.5.1", {"start": v(-780, 6480) * mm, "end": v(-180, 6480) * mm});
            skLineSegment(sketch, "E18.7.5.2", {"start": v(-780, 6880) * mm, "end": v(-780, 6480) * mm});
            skLineSegment(sketch, "E18.7.5.3", {"start": v(-180, 6880) * mm, "end": v(-180, 6480) * mm});
            skLineSegment(sketch, "E18.7.6.0", {"start": v(-780, 6475) * mm, "end": v(-180, 6475) * mm});
            skLineSegment(sketch, "E18.7.6.1", {"start": v(-780, 6075) * mm, "end": v(-180, 6075) * mm});
            skLineSegment(sketch, "E18.7.6.2", {"start": v(-780, 6475) * mm, "end": v(-780, 6075) * mm});
            skLineSegment(sketch, "E18.7.6.3", {"start": v(-180, 6475) * mm, "end": v(-180, 6075) * mm});
            skLineSegment(sketch, "E18.7.7.0", {"start": v(-780, 6070) * mm, "end": v(-180, 6070) * mm});
            skLineSegment(sketch, "E18.7.7.1", {"start": v(-780, 5670) * mm, "end": v(-180, 5670) * mm});
            skLineSegment(sketch, "E18.7.7.2", {"start": v(-780, 6070) * mm, "end": v(-780, 5670) * mm});
            skLineSegment(sketch, "E18.7.7.3", {"start": v(-180, 6070) * mm, "end": v(-180, 5670) * mm});
            skLineSegment(sketch, "E18.7.8.0", {"start": v(-780, 5665) * mm, "end": v(-180, 5665) * mm});
            skLineSegment(sketch, "E18.7.8.1", {"start": v(-780, 5265) * mm, "end": v(-180, 5265) * mm});
            skLineSegment(sketch, "E18.7.8.2", {"start": v(-780, 5665) * mm, "end": v(-780, 5265) * mm});
            skLineSegment(sketch, "E18.7.8.3", {"start": v(-180, 5665) * mm, "end": v(-180, 5265) * mm});
            skLineSegment(sketch, "E18.7.9.0", {"start": v(-780, 5260) * mm, "end": v(-180, 5260) * mm});
            skLineSegment(sketch, "E18.7.9.2", {"start": v(-780, 5260) * mm, "end": v(-780, 4860) * mm});
            skLineSegment(sketch, "E18.7.10.2", {"start": v(-780, 4855) * mm, "end": v(-780, 4455) * mm});
            skLineSegment(sketch, "E18.7.11.2", {"start": v(-780, 4450) * mm, "end": v(-780, 4050) * mm});
            skLineSegment(sketch, "E18.8.0.0", {"start": v(-175, 8905) * mm, "end": v(425, 8905) * mm});
            skLineSegment(sketch, "E18.8.0.1", {"start": v(-175, 8505) * mm, "end": v(425, 8505) * mm});
            skLineSegment(sketch, "E18.8.0.2", {"start": v(-175, 8905) * mm, "end": v(-175, 8505) * mm});
            skLineSegment(sketch, "E18.8.0.3", {"start": v(425, 8905) * mm, "end": v(425, 8505) * mm});
            skLineSegment(sketch, "E18.8.1.0", {"start": v(-175, 8500) * mm, "end": v(425, 8500) * mm});
            skLineSegment(sketch, "E18.8.1.1", {"start": v(-175, 8100) * mm, "end": v(425, 8100) * mm});
            skLineSegment(sketch, "E18.8.1.2", {"start": v(-175, 8500) * mm, "end": v(-175, 8100) * mm});
            skLineSegment(sketch, "E18.8.1.3", {"start": v(425, 8500) * mm, "end": v(425, 8100) * mm});
            skLineSegment(sketch, "E18.8.2.0", {"start": v(-175, 8095) * mm, "end": v(425, 8095) * mm});
            skLineSegment(sketch, "E18.8.2.1", {"start": v(-175, 7695) * mm, "end": v(425, 7695) * mm});
            skLineSegment(sketch, "E18.8.2.2", {"start": v(-175, 8095) * mm, "end": v(-175, 7695) * mm});
            skLineSegment(sketch, "E18.8.2.3", {"start": v(425, 8095) * mm, "end": v(425, 7695) * mm});
            skLineSegment(sketch, "E18.8.3.0", {"start": v(-175, 7690) * mm, "end": v(425, 7690) * mm});
            skLineSegment(sketch, "E18.8.3.1", {"start": v(-175, 7290) * mm, "end": v(425, 7290) * mm});
            skLineSegment(sketch, "E18.8.3.2", {"start": v(-175, 7690) * mm, "end": v(-175, 7290) * mm});
            skLineSegment(sketch, "E18.8.3.3", {"start": v(425, 7690) * mm, "end": v(425, 7290) * mm});
            skLineSegment(sketch, "E18.8.4.0", {"start": v(-175, 7285) * mm, "end": v(425, 7285) * mm});
            skLineSegment(sketch, "E18.8.4.1", {"start": v(-175, 6885) * mm, "end": v(425, 6885) * mm});
            skLineSegment(sketch, "E18.8.4.2", {"start": v(-175, 7285) * mm, "end": v(-175, 6885) * mm});
            skLineSegment(sketch, "E18.8.4.3", {"start": v(425, 7285) * mm, "end": v(425, 6885) * mm});
            skLineSegment(sketch, "E18.8.5.0", {"start": v(-175, 6880) * mm, "end": v(425, 6880) * mm});
            skLineSegment(sketch, "E18.8.5.1", {"start": v(-175, 6480) * mm, "end": v(425, 6480) * mm});
            skLineSegment(sketch, "E18.8.5.2", {"start": v(-175, 6880) * mm, "end": v(-175, 6480) * mm});
            skLineSegment(sketch, "E18.8.5.3", {"start": v(425, 6880) * mm, "end": v(425, 6480) * mm});
            skLineSegment(sketch, "E18.8.6.0", {"start": v(-175, 6475) * mm, "end": v(425, 6475) * mm});
            skLineSegment(sketch, "E18.8.6.1", {"start": v(-175, 6075) * mm, "end": v(425, 6075) * mm});
            skLineSegment(sketch, "E18.8.6.2", {"start": v(-175, 6475) * mm, "end": v(-175, 6075) * mm});
            skLineSegment(sketch, "E18.8.6.3", {"start": v(425, 6475) * mm, "end": v(425, 6075) * mm});
            skLineSegment(sketch, "E18.8.7.0", {"start": v(-175, 6070) * mm, "end": v(425, 6070) * mm});
            skLineSegment(sketch, "E18.8.7.1", {"start": v(-175, 5670) * mm, "end": v(425, 5670) * mm});
            skLineSegment(sketch, "E18.8.7.2", {"start": v(-175, 6070) * mm, "end": v(-175, 5670) * mm});
            skLineSegment(sketch, "E18.8.7.3", {"start": v(425, 6070) * mm, "end": v(425, 5670) * mm});
            skLineSegment(sketch, "E18.8.8.0", {"start": v(-175, 5665) * mm, "end": v(425, 5665) * mm});
            skLineSegment(sketch, "E18.8.8.1", {"start": v(-175, 5265) * mm, "end": v(425, 5265) * mm});
            skLineSegment(sketch, "E18.8.8.2", {"start": v(-175, 5665) * mm, "end": v(-175, 5265) * mm});
            skLineSegment(sketch, "E18.8.8.3", {"start": v(425, 5665) * mm, "end": v(425, 5265) * mm});
            skLineSegment(sketch, "E18.8.9.0", {"start": v(-175, 5260) * mm, "end": v(425, 5260) * mm});
            skLineSegment(sketch, "E18.9.0.0", {"start": v(430, 8905) * mm, "end": v(1030, 8905) * mm});
            skLineSegment(sketch, "E18.9.0.1", {"start": v(430, 8505) * mm, "end": v(1030, 8505) * mm});
            skLineSegment(sketch, "E18.9.0.2", {"start": v(430, 8905) * mm, "end": v(430, 8505) * mm});
            skLineSegment(sketch, "E18.9.0.3", {"start": v(1030, 8905) * mm, "end": v(1030, 8505) * mm});
            skLineSegment(sketch, "E18.9.1.0", {"start": v(430, 8500) * mm, "end": v(1030, 8500) * mm});
            skLineSegment(sketch, "E18.9.1.1", {"start": v(430, 8100) * mm, "end": v(1030, 8100) * mm});
            skLineSegment(sketch, "E18.9.1.2", {"start": v(430, 8500) * mm, "end": v(430, 8100) * mm});
            skLineSegment(sketch, "E18.9.1.3", {"start": v(1030, 8500) * mm, "end": v(1030, 8100) * mm});
            skLineSegment(sketch, "E18.9.2.0", {"start": v(430, 8095) * mm, "end": v(1030, 8095) * mm});
            skLineSegment(sketch, "E18.9.2.1", {"start": v(430, 7695) * mm, "end": v(1030, 7695) * mm});
            skLineSegment(sketch, "E18.9.2.2", {"start": v(430, 8095) * mm, "end": v(430, 7695) * mm});
            skLineSegment(sketch, "E18.9.2.3", {"start": v(1030, 8095) * mm, "end": v(1030, 7695) * mm});
            skLineSegment(sketch, "E18.9.3.0", {"start": v(430, 7690) * mm, "end": v(1030, 7690) * mm});
            skLineSegment(sketch, "E18.9.3.1", {"start": v(430, 7290) * mm, "end": v(1030, 7290) * mm});
            skLineSegment(sketch, "E18.9.3.2", {"start": v(430, 7690) * mm, "end": v(430, 7290) * mm});
            skLineSegment(sketch, "E18.9.3.3", {"start": v(1030, 7690) * mm, "end": v(1030, 7290) * mm});
            skLineSegment(sketch, "E18.9.4.0", {"start": v(430, 7285) * mm, "end": v(1030, 7285) * mm});
            skLineSegment(sketch, "E18.9.4.1", {"start": v(430, 6885) * mm, "end": v(1030, 6885) * mm});
            skLineSegment(sketch, "E18.9.4.2", {"start": v(430, 7285) * mm, "end": v(430, 6885) * mm});
            skLineSegment(sketch, "E18.9.4.3", {"start": v(1030, 7285) * mm, "end": v(1030, 6885) * mm});
            skLineSegment(sketch, "E18.9.5.0", {"start": v(430, 6880) * mm, "end": v(1030, 6880) * mm});
            skLineSegment(sketch, "E18.9.5.1", {"start": v(430, 6480) * mm, "end": v(1030, 6480) * mm});
            skLineSegment(sketch, "E18.9.5.2", {"start": v(430, 6880) * mm, "end": v(430, 6480) * mm});
            skLineSegment(sketch, "E18.9.5.3", {"start": v(1030, 6880) * mm, "end": v(1030, 6480) * mm});
            skLineSegment(sketch, "E18.9.6.0", {"start": v(430, 6475) * mm, "end": v(1030, 6475) * mm});
            skLineSegment(sketch, "E18.9.6.1", {"start": v(430, 6075) * mm, "end": v(1030, 6075) * mm});
            skLineSegment(sketch, "E18.9.6.2", {"start": v(430, 6475) * mm, "end": v(430, 6075) * mm});
            skLineSegment(sketch, "E18.9.6.3", {"start": v(1030, 6475) * mm, "end": v(1030, 6075) * mm});
            skLineSegment(sketch, "E18.9.7.0", {"start": v(430, 6070) * mm, "end": v(1030, 6070) * mm});
            skLineSegment(sketch, "E18.9.7.1", {"start": v(430, 5670) * mm, "end": v(1030, 5670) * mm});
            skLineSegment(sketch, "E18.9.7.2", {"start": v(430, 6070) * mm, "end": v(430, 5670) * mm});
            skLineSegment(sketch, "E18.9.7.3", {"start": v(1030, 6070) * mm, "end": v(1030, 5670) * mm});
            skLineSegment(sketch, "E18.9.8.0", {"start": v(430, 5665) * mm, "end": v(1030, 5665) * mm});
            skLineSegment(sketch, "E18.9.8.1", {"start": v(430, 5265) * mm, "end": v(1030, 5265) * mm});
            skLineSegment(sketch, "E18.9.8.2", {"start": v(430, 5665) * mm, "end": v(430, 5265) * mm});
            skLineSegment(sketch, "E18.9.8.3", {"start": v(1030, 5665) * mm, "end": v(1030, 5265) * mm});
            skLineSegment(sketch, "E18.9.9.0", {"start": v(430, 5260) * mm, "end": v(1030, 5260) * mm});
            skLineSegment(sketch, "E18.10.0.0", {"start": v(1035, 8905) * mm, "end": v(1635, 8905) * mm});
            skLineSegment(sketch, "E18.10.0.1", {"start": v(1035, 8505) * mm, "end": v(1635, 8505) * mm});
            skLineSegment(sketch, "E18.10.0.2", {"start": v(1035, 8905) * mm, "end": v(1035, 8505) * mm});
            skLineSegment(sketch, "E18.10.0.3", {"start": v(1635, 8905) * mm, "end": v(1635, 8505) * mm});
            skLineSegment(sketch, "E18.10.1.0", {"start": v(1035, 8500) * mm, "end": v(1635, 8500) * mm});
            skLineSegment(sketch, "E18.10.1.1", {"start": v(1035, 8100) * mm, "end": v(1635, 8100) * mm});
            skLineSegment(sketch, "E18.10.1.2", {"start": v(1035, 8500) * mm, "end": v(1035, 8100) * mm});
            skLineSegment(sketch, "E18.10.1.3", {"start": v(1635, 8500) * mm, "end": v(1635, 8100) * mm});
            skLineSegment(sketch, "E18.10.2.0", {"start": v(1035, 8095) * mm, "end": v(1635, 8095) * mm});
            skLineSegment(sketch, "E18.10.2.1", {"start": v(1035, 7695) * mm, "end": v(1635, 7695) * mm});
            skLineSegment(sketch, "E18.10.2.2", {"start": v(1035, 8095) * mm, "end": v(1035, 7695) * mm});
            skLineSegment(sketch, "E18.10.2.3", {"start": v(1635, 8095) * mm, "end": v(1635, 7695) * mm});
            skLineSegment(sketch, "E18.10.3.0", {"start": v(1035, 7690) * mm, "end": v(1635, 7690) * mm});
            skLineSegment(sketch, "E18.10.3.1", {"start": v(1035, 7290) * mm, "end": v(1635, 7290) * mm});
            skLineSegment(sketch, "E18.10.3.2", {"start": v(1035, 7690) * mm, "end": v(1035, 7290) * mm});
            skLineSegment(sketch, "E18.10.3.3", {"start": v(1635, 7690) * mm, "end": v(1635, 7290) * mm});
            skLineSegment(sketch, "E18.10.4.0", {"start": v(1035, 7285) * mm, "end": v(1635, 7285) * mm});
            skLineSegment(sketch, "E18.10.4.1", {"start": v(1035, 6885) * mm, "end": v(1635, 6885) * mm});
            skLineSegment(sketch, "E18.10.4.2", {"start": v(1035, 7285) * mm, "end": v(1035, 6885) * mm});
            skLineSegment(sketch, "E18.10.4.3", {"start": v(1635, 7285) * mm, "end": v(1635, 6885) * mm});
            skLineSegment(sketch, "E18.10.5.0", {"start": v(1035, 6880) * mm, "end": v(1635, 6880) * mm});
            skLineSegment(sketch, "E18.10.5.1", {"start": v(1035, 6480) * mm, "end": v(1635, 6480) * mm});
            skLineSegment(sketch, "E18.10.5.2", {"start": v(1035, 6880) * mm, "end": v(1035, 6480) * mm});
            skLineSegment(sketch, "E18.10.5.3", {"start": v(1635, 6880) * mm, "end": v(1635, 6480) * mm});
            skLineSegment(sketch, "E18.10.6.0", {"start": v(1035, 6475) * mm, "end": v(1635, 6475) * mm});
            skLineSegment(sketch, "E18.10.6.1", {"start": v(1035, 6075) * mm, "end": v(1635, 6075) * mm});
            skLineSegment(sketch, "E18.10.6.2", {"start": v(1035, 6475) * mm, "end": v(1035, 6075) * mm});
            skLineSegment(sketch, "E18.10.6.3", {"start": v(1635, 6475) * mm, "end": v(1635, 6075) * mm});
            skLineSegment(sketch, "E18.10.7.0", {"start": v(1035, 6070) * mm, "end": v(1635, 6070) * mm});
            skLineSegment(sketch, "E18.10.7.1", {"start": v(1035, 5670) * mm, "end": v(1635, 5670) * mm});
            skLineSegment(sketch, "E18.10.7.2", {"start": v(1035, 6070) * mm, "end": v(1035, 5670) * mm});
            skLineSegment(sketch, "E18.10.7.3", {"start": v(1635, 6070) * mm, "end": v(1635, 5670) * mm});
            skLineSegment(sketch, "E18.10.8.0", {"start": v(1035, 5665) * mm, "end": v(1635, 5665) * mm});
            skLineSegment(sketch, "E18.10.8.1", {"start": v(1035, 5265) * mm, "end": v(1635, 5265) * mm});
            skLineSegment(sketch, "E18.10.8.2", {"start": v(1035, 5665) * mm, "end": v(1035, 5265) * mm});
            skLineSegment(sketch, "E18.10.8.3", {"start": v(1635, 5665) * mm, "end": v(1635, 5265) * mm});
            skLineSegment(sketch, "E18.10.9.0", {"start": v(1035, 5260) * mm, "end": v(1635, 5260) * mm});
            skLineSegment(sketch, "E18.11.0.0", {"start": v(1640, 8905) * mm, "end": v(2240, 8905) * mm});
            skLineSegment(sketch, "E18.11.0.1", {"start": v(1640, 8505) * mm, "end": v(2240, 8505) * mm});
            skLineSegment(sketch, "E18.11.0.2", {"start": v(1640, 8905) * mm, "end": v(1640, 8505) * mm});
            skLineSegment(sketch, "E18.11.0.3", {"start": v(2240, 8905) * mm, "end": v(2240, 8505) * mm});
            skLineSegment(sketch, "E18.11.1.0", {"start": v(1640, 8500) * mm, "end": v(2240, 8500) * mm});
            skLineSegment(sketch, "E18.11.1.1", {"start": v(1640, 8100) * mm, "end": v(2240, 8100) * mm});
            skLineSegment(sketch, "E18.11.1.2", {"start": v(1640, 8500) * mm, "end": v(1640, 8100) * mm});
            skLineSegment(sketch, "E18.11.1.3", {"start": v(2240, 8500) * mm, "end": v(2240, 8100) * mm});
            skLineSegment(sketch, "E18.11.2.0", {"start": v(1640, 8095) * mm, "end": v(2240, 8095) * mm});
            skLineSegment(sketch, "E18.11.2.1", {"start": v(1640, 7695) * mm, "end": v(2240, 7695) * mm});
            skLineSegment(sketch, "E18.11.2.2", {"start": v(1640, 8095) * mm, "end": v(1640, 7695) * mm});
            skLineSegment(sketch, "E18.11.2.3", {"start": v(2240, 8095) * mm, "end": v(2240, 7695) * mm});
            skLineSegment(sketch, "E18.11.3.0", {"start": v(1640, 7690) * mm, "end": v(2240, 7690) * mm});
            skLineSegment(sketch, "E18.11.3.1", {"start": v(1640, 7290) * mm, "end": v(2240, 7290) * mm});
            skLineSegment(sketch, "E18.11.3.2", {"start": v(1640, 7690) * mm, "end": v(1640, 7290) * mm});
            skLineSegment(sketch, "E18.11.3.3", {"start": v(2240, 7690) * mm, "end": v(2240, 7290) * mm});
            skLineSegment(sketch, "E18.11.4.0", {"start": v(1640, 7285) * mm, "end": v(2240, 7285) * mm});
            skLineSegment(sketch, "E18.11.4.1", {"start": v(1640, 6885) * mm, "end": v(2240, 6885) * mm});
            skLineSegment(sketch, "E18.11.4.2", {"start": v(1640, 7285) * mm, "end": v(1640, 6885) * mm});
            skLineSegment(sketch, "E18.11.4.3", {"start": v(2240, 7285) * mm, "end": v(2240, 6885) * mm});
            skLineSegment(sketch, "E18.11.5.0", {"start": v(1640, 6880) * mm, "end": v(2240, 6880) * mm});
            skLineSegment(sketch, "E18.11.5.1", {"start": v(1640, 6480) * mm, "end": v(2240, 6480) * mm});
            skLineSegment(sketch, "E18.11.5.2", {"start": v(1640, 6880) * mm, "end": v(1640, 6480) * mm});
            skLineSegment(sketch, "E18.11.5.3", {"start": v(2240, 6880) * mm, "end": v(2240, 6480) * mm});
            skLineSegment(sketch, "E18.11.6.0", {"start": v(1640, 6475) * mm, "end": v(2240, 6475) * mm});
            skLineSegment(sketch, "E18.11.6.1", {"start": v(1640, 6075) * mm, "end": v(2240, 6075) * mm});
            skLineSegment(sketch, "E18.11.6.2", {"start": v(1640, 6475) * mm, "end": v(1640, 6075) * mm});
            skLineSegment(sketch, "E18.11.6.3", {"start": v(2240, 6475) * mm, "end": v(2240, 6075) * mm});
            skLineSegment(sketch, "E18.11.7.0", {"start": v(1640, 6070) * mm, "end": v(2240, 6070) * mm});
            skLineSegment(sketch, "E18.11.7.1", {"start": v(1640, 5670) * mm, "end": v(2240, 5670) * mm});
            skLineSegment(sketch, "E18.11.7.2", {"start": v(1640, 6070) * mm, "end": v(1640, 5670) * mm});
            skLineSegment(sketch, "E18.11.7.3", {"start": v(2240, 6070) * mm, "end": v(2240, 5670) * mm});
            skLineSegment(sketch, "E18.11.8.0", {"start": v(1640, 5665) * mm, "end": v(2240, 5665) * mm});
            skLineSegment(sketch, "E18.11.8.1", {"start": v(1640, 5265) * mm, "end": v(2240, 5265) * mm});
            skLineSegment(sketch, "E18.11.8.2", {"start": v(1640, 5665) * mm, "end": v(1640, 5265) * mm});
            skLineSegment(sketch, "E18.11.8.3", {"start": v(2240, 5665) * mm, "end": v(2240, 5265) * mm});
            skLineSegment(sketch, "E18.11.9.0", {"start": v(1640, 5260) * mm, "end": v(2240, 5260) * mm});
            skLineSegment(sketch, "E18.direction1", {"start": v(-5015, 8505) * mm, "end": v(-4410, 8505) * mm, "construction": true});
            skLineSegment(sketch, "E18.direction2", {"start": v(-5015, 8505) * mm, "end": v(-5015, 8100) * mm, "construction": true});
            skSolve(sketch);
        }
        {
            var Q0;
            Q0 = qSketchRegion(id + "F6", true);
            extrude(context, id + "F7", {"entities" : qUnion([Q0]), "operationType" : NewBodyOperationType.ADD, "depth" : 25 * mm, "offsetDistance" : 25 * mm});
        }
    });
